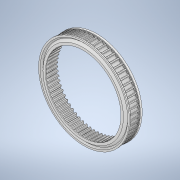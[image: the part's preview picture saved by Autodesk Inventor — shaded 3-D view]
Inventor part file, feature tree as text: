
AUTODESK INVENTOR PART (.ipt)
format: ipt  version: 2020 (Build 240168000, 168)  size: 1,402,880 bytes
history: native  units: mm (DEFAULTED — no unit token found)
features: sketch x6, extrude x4, plane x4, other x3, revolve x3, chamfer x1, mirror x1
ambient origin geometry x8: Origin, YZ Plane, XZ Plane, XY Plane, X Axis, Y Axis, Z Axis, Center Point
bodies: Solid1 (feature_tree)
feature tree (22):
  extrude  "Extrusion1"  Depth=12.7mm TaperAngle=0.0deg
  plane  "Work Plane1"
  plane  "Work Plane2"
  plane  "Work Plane3"
  other  "Spur Gear"
  sketch  "Sketch3"  dims[d6=0.0mm d7=0.490874mm d9=0.0mm]
  extrude  "Extrusion2"  Depth=76.2mm TaperAngle=0.0deg
  extrude  "Extrusion3"  TaperAngle=0.0deg  [1 undecoded]
  extrude  "Extrusion7"  TaperAngle=0.0deg  [1 undecoded]
  sketch  "Sketch7"  dims[d14=0.0mm d15=30.48mm d16=0.0mm]
  revolve  "Revolution3"  [1 undecoded]
  chamfer  "Chamfer2"  Distance=1.047198mm
  plane  "Work Plane5"
  revolve  "Revolution4"  [1 undecoded]
  mirror  "Mirror2"
  revolve  "Revolution5"  Angle=360.0deg
  sketch  "Sketch1"  dims[d0=92.9005mm d1=12.7mm d2=0.0mm]
  sketch  "Sketch2"  dims[d3=81.28mm d4=76.2mm d5=0.0mm]
  other  "Srf1"
  sketch  "Sketch8"  dims[d17=0.0mm d18=0.0mm d19=30.48mm d20=94.35mm]
  sketch  "Sketch9"  dims[d21=90.19mm d23=1.047198mm d24=3.05mm d26=600.0mm d28=360.0deg d30=25.4mm d31=0.0mm d32=25.4mm d33=0.0mm d34=0.01mm d35=0.01mm d52=0.9mm d58=44.45mm d59=13.49375mm d61=90.0deg d62=3.175mm d63=95.25mm d64=1.5875mm d65=0.0mm d66=0.396875mm d67=3.175mm d68=45.0deg d70=90.0deg d73=39.6875mm d74=0.79375mm d75=90.0deg]
  other  "Pitch Diameter"
note: 4 required parameter values undecoded (feature->parameter linkage not recoverable at this tier; creation-order binding heuristic only, values carry confidence <= 0.55)